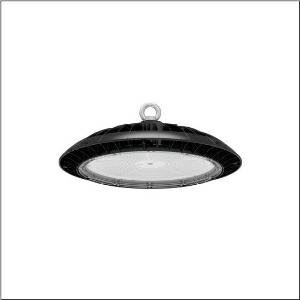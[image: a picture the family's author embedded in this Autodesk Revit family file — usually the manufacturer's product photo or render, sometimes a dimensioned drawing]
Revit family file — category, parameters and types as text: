
# Revit family: highbay_42-l_51hp32mb4mma
name_source: partatom
category: Lighting Fixtures
units: mm (PartAtom-declared; Revit-internal decimal feet)

## family parameters
Cut with Voids When Loaded = No
Host = Face
Light Source = No
Part Type = Normal
Room Calculation Point = No
Round Connector Dimension = Use Diameter
Shared = No

## types (1)
- --- (1 x LED, 28000 lm, 175 W, 4000K)
    Apparent Load = 175 VA
    CIE Flux Codes = 49 82 98 100 100
    Color Rendering = 80
    Color Temperature = 4000K
    Default Elevation = 1800 mm
    Description = Highbay 42-L, LED high bay luminaire, primary light control with lens, of PC, primary optical cover: cover panel, of PC, transparent, light emission: direct distribution, primary light characteristic: rotationally symmetric, installation type: suspended mounting, surface-mounted, LED, rated luminous flux: 28.000lm, luminous efficacy: 160lm/W, light colour: 840, colour temperature: 4000K, control gear: ON/OFF Multilumen, with cable, 3x 1.0mm², free wire ends, mains connection: 230V, AC, 50Hz, cable length: 1,5m, rated input power: 175W, housing, rotationally symmetric, of diecast aluminium, black, with hook on luminaire side, diameter: 305mm, height: 117mm, protection rating (complete): IP65, insulation class (complete): insulation class I (protective earthing), certification: CE, UKCA, protection symbol: D, impact resistance: IK08, permissible operating ambient temperature: -20..+40°C, corresponds to IFS (International Featured Standards) requirements for safety and quality in the food industry, packaging unit: 1 piece
    Height = 117 mm
    Lamp = 1 x LED
    Lamp Light Flux = 28000 lm
    Lamp Power = 175 W
    Lamp count = 1
    Length = 305 mm
    Luminous efficacy = 160 lm/W
    Manufacturer = Siteco
    ModVariant = No
    Model = 51HP32MB4MMA
    Mounting Place = Ceiling
    Mounting Type = Pendant
    Number of Poles = 1
    OnlyDefault = Yes
    Power Factor = 1
    Product Name = Highbay 42-L
    Product group = LED high bay luminaire
    ProductGroupID = 903
    Protection Class = Protection class I
    Protection Degree = IP 65
    RLX_Detail_Level = 1
    RLX_Emergency_Light_Flux = 0 lm
    RLX_Emergency_Type = 0
    RLX_Emergency_Type_DB = No
    RlxData = <blob elided: 286333 chars, md5=7db9c3a2>
    Socket = socket
    Standby Power = 0 W
    System Light Flux = 28000 lm
    System Power = 175 W
    Type Comments = factory setting: luminous flux: 100 % | (OFF | OFF | OFF)
    Type Image = l_1003932.jpg
    URL = http://relux.com
    VarID = @adj_197658
    Voltage = 0 V
    Weight = 0.00 kg
    Width = 0 mm  [stored 0 ft]

note: [stored X ft] marks values corroborated as IEEE doubles in the binary element streams (Revit-internal decimal feet)

## geometry (parser evidence)
native form markers: Blend x4, Sweep x11
no freeform markers — native parametric forms only
